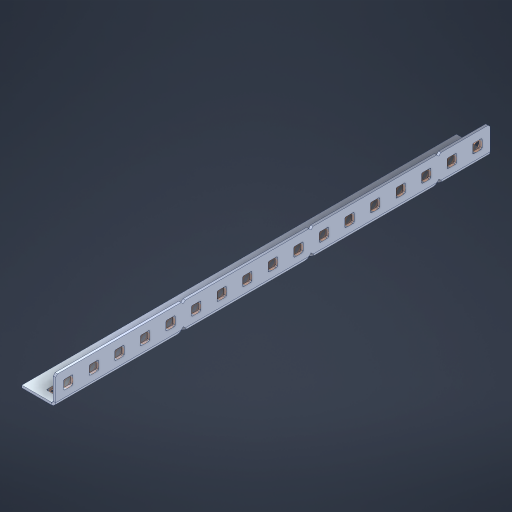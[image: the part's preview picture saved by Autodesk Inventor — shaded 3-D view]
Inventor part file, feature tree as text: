
AUTODESK INVENTOR PART (.ipt)
format: ipt  version: 2023 (Build 270158000, 158)  size: 700,416 bytes
history: native  units: in
note: dims shown in document units (in); Inventor stores cm internally (conversion verified against a paired STEP export)
features: other x39, extrude x33, sheet_metal_op x10, sketch x8, mirror x1, pattern_linear x1, chamfer x1
ambient origin geometry x8: Origin, YZ Plane, XZ Plane, XY Plane, X Axis, Y Axis, Z Axis, Center Point
bodies: Solid1 (feature_tree), Body (feature_tree)
feature tree (93):
  other  "Flange Pattern Plane"
  sheet_metal_op  "Flange Pattern"
  sheet_metal_op  "Body Pattern"
  other  "Arc Length"
  mirror  "Notch Mirror"
  pattern_linear  "Notch Pattern"  Spacing1=0.1875in  [1 undecoded]
  chamfer  "End Chamfer"
  extrude  "Half Cut"  Depth=0.0469in
  sketch  "Sketch1"  dims[d0=2.5in]
  other  "Plate1"
  sketch  "Sketch2"  dims[d1=8.5in]
  other  "Plate2"
  sheet_metal_op  "Bend1"
  sheet_metal_op  "Corner1"
  sketch  "Sketch3"  dims[d2=0.0469in]
  other  "Flange Pattern Sketch"
  sketch  "Sketch7"  dims[d3=0.0469in]
  other  "Srf1"
  other  "Srf2"
  sketch  "Sketch8"  dims[d4=0.0234in]
  sketch  "Sketch9"  dims[d5=0.0938in]
  other  "Srf91"
  sheet_metal_op  "Body Pattern Sketch"
  other  "Srf92"
  sketch  "Sketch13"  dims[d6=0.0469in]
  sketch  "Sketch14"  dims[d7=0.5in d8=90.0deg d9=0.0312in d10=0.1875in d11=0.0469in d12=0.0469in d16=0.182in d17=0.02in d18=0.0469in d19=0.0in d20=0.25in d21=0.25in d46=0.172in d47=1.0in d48=0.0in d49=0.182in d50=0.02in d51=0.25in d52=0.25in d53=0.0469in d54=0.0in d55=0.172in d56=1.0in d57=0.0in d60=6.6929in d62=0.5in d63=0.3937in d65=0.5in d85=0.1227in d86=0.1659in d88=0.04in d89=0.0469in d90=0.0in d91=0.04in d92=0.0491in d95=2.5in d96=0.04in d97=0.25in d98=45.0deg d101=0.0in d102=2.497in d131=0.5in d132=6.6929in d134=0.5in d139=0.5in]
  other  "Srf856"
  other  "Srf1310"
  other  "Srf1311"
  other  "Srf1312"
  other  "Srf1376"
  other  "Srf1377"
  other  "Srf1728"
  other  "Srf1755"
  other  "Srf1878"
  other  "Srf1879"
  other  "Srf1880"
  other  "Srf1881"
  other  "Srf1882"
  other  "Srf1883"
  other  "Srf1884"
  other  "Srf1885"
  other  "Srf1886"
  other  "Srf1887"
  other  "Srf1888"
  other  "Srf1942"
  other  "Srf1943"
  other  "Srf1944"
  other  "Srf1945"
  other  "Srf1946"
  other  "Srf1947"
  other  "Srf1948"
  other  "Srf1949"
  other  "Srf1950"
  other  "Srf1951"
  other  "Srf1952"
  sheet_metal_op  "Flange Stamp"
  sheet_metal_op  "Flange Circle"
  sheet_metal_op  "Body Stamp"
  sheet_metal_op  "Body Circle"
  sheet_metal_op  "Notch"
  extrude  "ExtrusionSrf2"  Depth=0.0469in
  extrude  "ExtrusionSrf92"  Depth=0.5in
  extrude  "ExtrusionSrf856"  Depth=0.02in
  extrude  "ExtrusionSrf1310"  Depth=0.0469in
  extrude  "ExtrusionSrf1311"  TaperAngle=0.0deg  [1 undecoded]
  extrude  "ExtrusionSrf1312"  Depth=0.5in
  extrude  "ExtrusionSrf1376"  Depth=0.5in
  extrude  "ExtrusionSrf1377"  Depth=0.5in
  extrude  "ExtrusionSrf1728"  Depth=0.5in TaperAngle=0.0deg
  extrude  "ExtrusionSrf1755"  Depth=0.5in
  extrude  "ExtrusionSrf1878"  Depth=0.02in
  extrude  "ExtrusionSrf1879"  Depth=0.5in
  extrude  "ExtrusionSrf1880"  Depth=0.5in
  extrude  "ExtrusionSrf1881"  Depth=0.0469in
  extrude  "ExtrusionSrf1882"  TaperAngle=0.0deg  [1 undecoded]
  extrude  "ExtrusionSrf1883"  Depth=0.5in
  extrude  "ExtrusionSrf1884"  Depth=0.5in TaperAngle=0.0deg
  extrude  "ExtrusionSrf1885"  Depth=0.5in
  extrude  "ExtrusionSrf1886"  Depth=0.5in
  extrude  "ExtrusionSrf1887"  Depth=0.5in
  extrude  "ExtrusionSrf1888"  Depth=0.5in
  extrude  "ExtrusionSrf1942"  Depth=0.5in
  extrude  "ExtrusionSrf1943"  Depth=0.0469in
  extrude  "ExtrusionSrf1944"  TaperAngle=0.0deg  [1 undecoded]
  extrude  "ExtrusionSrf1945"  Depth=0.5in
  extrude  "ExtrusionSrf1946"  Depth=0.5in
  extrude  "ExtrusionSrf1947"  Depth=0.5in
  extrude  "ExtrusionSrf1948"  Depth=0.5in TaperAngle=45.0deg
  extrude  "ExtrusionSrf1949"  TaperAngle=0.0deg  [1 undecoded]
  extrude  "ExtrusionSrf1950"  Depth=0.5in
  extrude  "ExtrusionSrf1951"  Depth=0.5in
  extrude  "ExtrusionSrf1952"  Depth=0.5in
note: 5 required parameter values undecoded (feature->parameter linkage not recoverable at this tier; creation-order binding heuristic only, values carry confidence <= 0.55)
